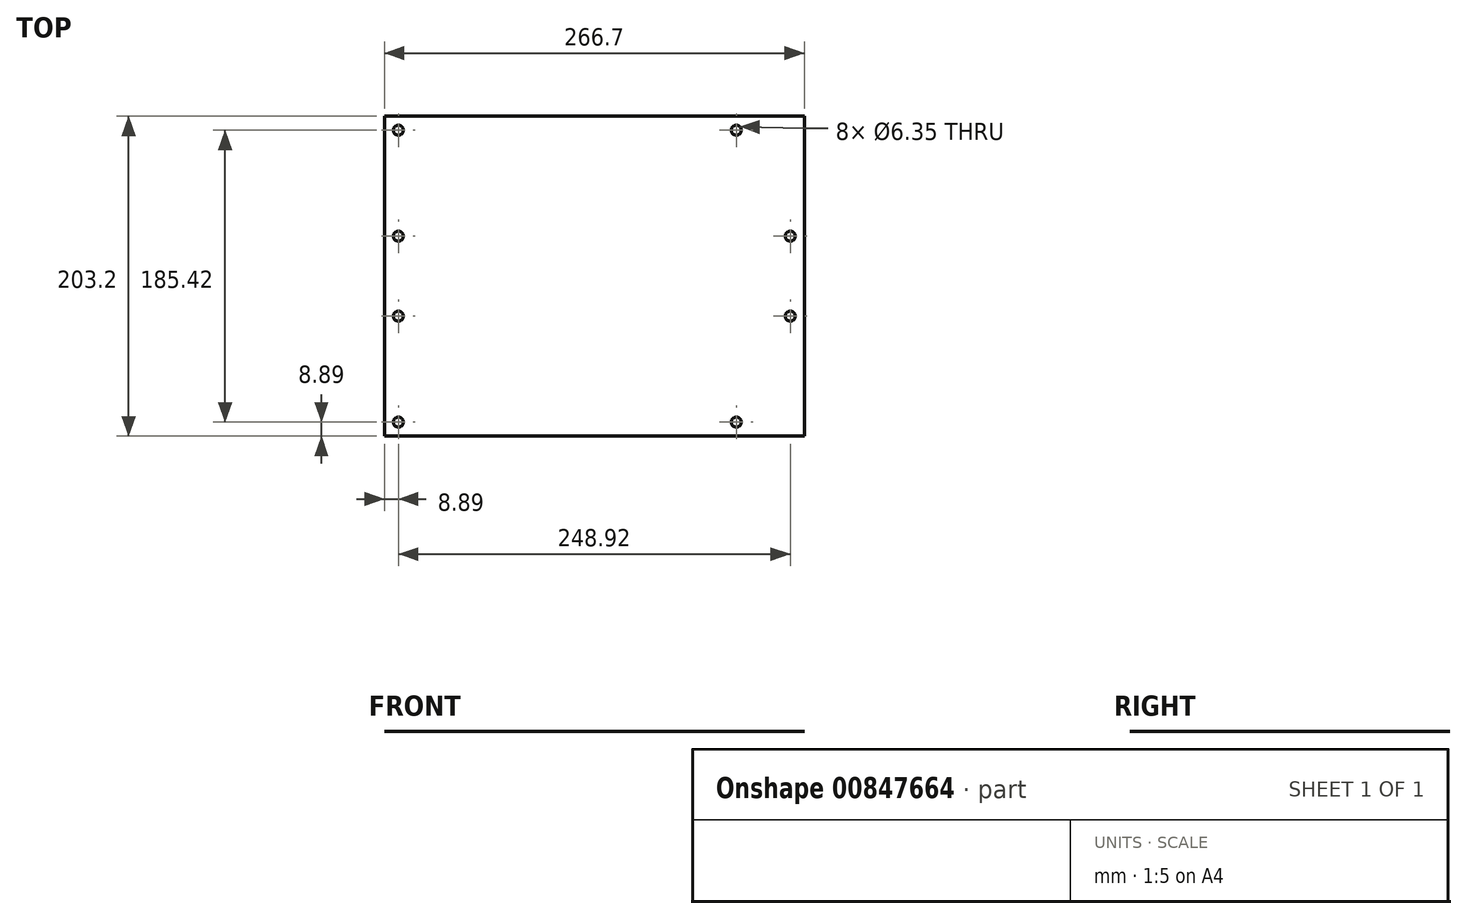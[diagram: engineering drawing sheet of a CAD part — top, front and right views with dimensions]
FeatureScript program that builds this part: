
annotation { "Feature Type Name" : "Feature", "Feature Type Description" : "" }
export const myFeature = defineFeature(function(context is Context, id is Id, definition is map)
    precondition{}
    {
        {
            var Q0;
            Q0=qCreatedBy(makeId("Top.planeOp"),FACE);
            var sketch = newSketch(context, id + "F0", { "sketchPlane" : qUnion([Q0])});
            skLineSegment(sketch, "E0.bottom", {"start": v(133.35, -101.6) * mm, "end": v(-133.35, -101.6) * mm});
            skLineSegment(sketch, "E0.top", {"start": v(133.35, 101.6) * mm, "end": v(-133.35, 101.6) * mm});
            skLineSegment(sketch, "E0.left", {"start": v(133.35, -101.6) * mm, "end": v(133.35, 101.6) * mm});
            skLineSegment(sketch, "E0.right", {"start": v(-133.35, -101.6) * mm, "end": v(-133.35, 101.6) * mm});
            skPoint(sketch, "E0.middle", {"position": v(0, 0) * mm});
            skCircle(sketch, "E1", {"center": v(90.17, -92.7) * mm, "radius": 3.18 * mm});
            skCircle(sketch, "E2", {"center": v(90.17, 92.71) * mm, "radius": 3.18 * mm});
            skCircle(sketch, "E3", {"center": v(-124.46, 92.7) * mm, "radius": 3.18 * mm});
            skCircle(sketch, "E4", {"center": v(-124.46, -92.71) * mm, "radius": 3.18 * mm});
            skCircle(sketch, "E5", {"center": v(-124.46, -25.4) * mm, "radius": 3.18 * mm});
            skCircle(sketch, "E6", {"center": v(-124.46, 25.4) * mm, "radius": 3.18 * mm});
            skCircle(sketch, "E7", {"center": v(124.46, -25.4) * mm, "radius": 3.18 * mm});
            skCircle(sketch, "E8", {"center": v(124.46, 25.4) * mm, "radius": 3.18 * mm});
            skSolve(sketch);
        }
        {
            var Q0;
            Q0=makeQuery(id+"F0.imprint","IMPRINT",FACE,{"disambiguationData":[TD([[makeQuery(id+"F0.imprint","IMPRINT",EDGE,{"derivedFrom":sQuery(id+"F0.wireOp",EDGE,"E0.bottom")}),-1.0]])]});
            extrude(context, id + "F1", {"entities" : qUnion([Q0]), "depth" : 1 / 406.4 * mm, "offsetDistance" : 25.4 * mm});
        }
    });
